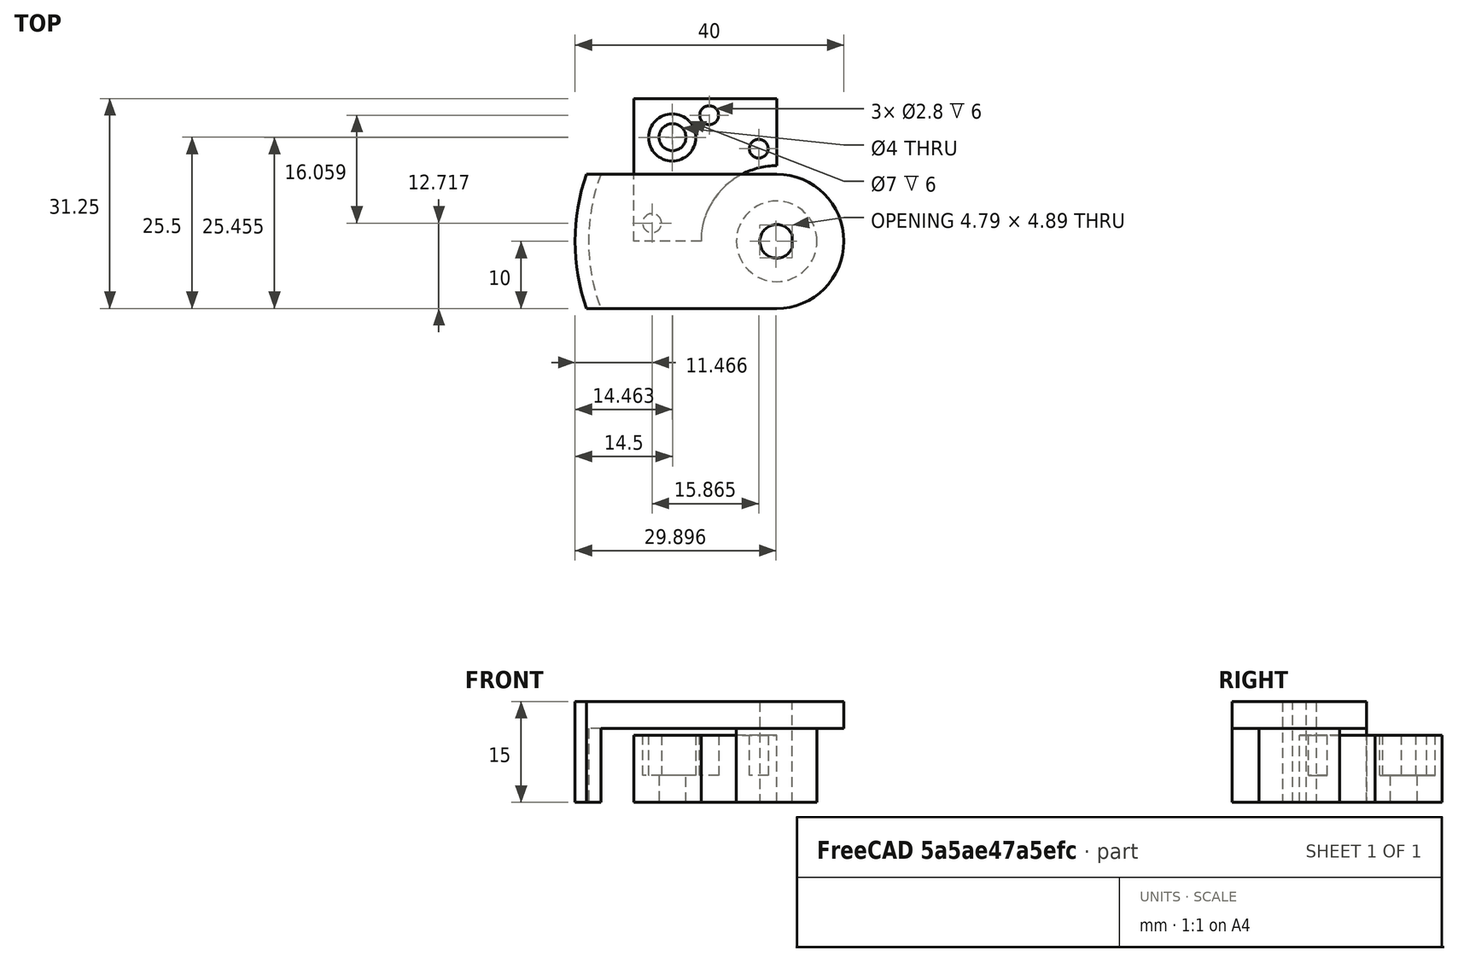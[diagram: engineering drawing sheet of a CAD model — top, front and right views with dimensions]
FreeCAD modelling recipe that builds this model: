
FCSTD DOCUMENT  (FreeCAD 0.19R)
Label: False_zaxisFlag
License: All rights reserved
LicenseURL: http://en.wikipedia.org/wiki/All_rights_reserved
objects: Sketcher::SketchObject×6, PartDesign::Pocket×3, PartDesign::Pad×2, PartDesign::Body×2, Mesh::Feature×2
note: 18 computed .brp shape members not serialized (recipe doc carries the construction recipe); baked Part::Feature solids carry a one-line shape summary decoded from their .brp

FEATURE [Sketcher::SketchObject] Sketch
  FullyConstrained = true
  MapMode = 5
  Support = -> [XY_Plane]
  sketch-geometry (6):
    g0: ArcOfCircle CenterX=0 CenterY=0 CenterZ=0 NormalX=0 NormalY=0 NormalZ=1 AngleXU=0 Radius=11.25 StartAngle=1.5708 EndAngle=3.14159
    g1: LineSegment StartX=-11.25 StartY=1.4e-15 StartZ=0 EndX=-21.25 EndY=0 EndZ=0
    g2: LineSegment StartX=-21.25 StartY=0 StartZ=0 EndX=-21.25 EndY=21.25 EndZ=0
    g3: LineSegment StartX=-21.25 StartY=21.25 StartZ=0 EndX=0 EndY=21.25 EndZ=0
    g4: LineSegment StartX=0 StartY=21.25 StartZ=0 EndX=7e-16 EndY=11.25 EndZ=0
    g5: Circle CenterX=-15.5 CenterY=15.5 CenterZ=0 NormalX=0 NormalY=0 NormalZ=1 AngleXU=0 Radius=2
  constraints (18):
    c: Coincident(g0,g-1)
    c: PointOnObject(g0,g-2)
    c: PointOnObject(g0,g-1)
    c: Coincident(g0,g1)
    c: Coincident(g1,g2)
    c: Vertical(g2)
    c: Coincident(g2,g3)
    c: PointOnObject(g3,g-2)
    c: Horizontal(g3)
    c: Coincident(g3,g4)
    c: Coincident(g4,g0)
    c: Diameter(g0) = 22.5
    c: Distance(g4) = 10
    c: Distance(g1) = 10
    c: PointOnObject(g1,g-1)
    c: DistanceX(g5) = -15.5
    c: DistanceY(g5) = 15.5
    c: Diameter(g5) = 4
FEATURE [PartDesign::Pad] Pad
  Direction = (1,1,1)
  Length = 10
  Length2 = 100
  Profile = -> Sketch
  Type = 0
FEATURE [Sketcher::SketchObject] Sketch001
  FullyConstrained = false
  MapMode = 5
  Placement = pos=(0,0,10) rot=(0,0,1;0rad)
  Support = -> [Pad]
  sketch-geometry (4):
    g0: LineSegment StartX=-19.7905 StartY=5 StartZ=0 EndX=-14.7905 EndY=5 EndZ=0
    g1: LineSegment StartX=-14.7905 StartY=5 StartZ=0 EndX=-14.7905 EndY=0 EndZ=0
    g2: LineSegment StartX=-14.7905 StartY=0 StartZ=0 EndX=-19.7905 EndY=0 EndZ=0
    g3: LineSegment StartX=-19.7905 StartY=0 StartZ=0 EndX=-19.7905 EndY=5 EndZ=0
  constraints (11):
    c: Coincident(g0,g1)
    c: Coincident(g1,g2)
    c: Coincident(g2,g3)
    c: Coincident(g3,g0)
    c: Horizontal(g0)
    c: Horizontal(g2)
    c: Vertical(g1)
    c: Vertical(g3)
    c: PointOnObject(g1,g-1)
    c: Distance(g0) = 5
    c: Distance(g1) = 5
FEATURE [Sketcher::SketchObject] Sketch002
  FullyConstrained = false
  MapMode = 5
  Placement = pos=(0,0,10) rot=(0,0,1;0rad)
  Support = -> [Pad]
  sketch-geometry (4):
    g0: Circle CenterX=-18.5342 CenterY=2.71688 CenterZ=0 NormalX=0 NormalY=0 NormalZ=1 AngleXU=0 Radius=1.4
    g1: Circle CenterX=-10.0417 CenterY=18.7754 CenterZ=0 NormalX=0 NormalY=0 NormalZ=1 AngleXU=0 Radius=1.4
    g2: Circle CenterX=-2.66872 CenterY=13.7957 CenterZ=0 NormalX=0 NormalY=0 NormalZ=1 AngleXU=0 Radius=1.4
    g3: Circle CenterX=-15.5368 CenterY=15.4549 CenterZ=0 NormalX=0 NormalY=0 NormalZ=1 AngleXU=0 Radius=3.5
  constraints (4):
    c: Diameter(g0) = 2.8
    c: Equal(g0,g2)
    c: Equal(g0,g1)
    c: Diameter(g3) = 7
FEATURE [PartDesign::Pocket] Pocket
  BaseFeature = -> Pad
  Length = 6
  Length2 = 100
  Profile = -> Sketch002
  Type = 0
FEATURE [PartDesign::Body] Body
  Group = -> [Sketch,Pad,Sketch001,Sketch002,Pocket]
  Origin = -> Origin
  Tip = -> Pocket
FEATURE [Mesh::Feature] Mesh  label="Pocket (Meshed)"
FEATURE [Sketcher::SketchObject] Sketch003
  FullyConstrained = true
  MapMode = 5
  Support = -> [XY_Plane001]
  sketch-geometry (4):
    g0: ArcOfCircle CenterX=0 CenterY=0 CenterZ=0 NormalX=0 NormalY=0 NormalZ=1 AngleXU=0 Radius=10 StartAngle=4.71239 EndAngle=7.85398
    g1: LineSegment StartX=-1.8e-15 StartY=-10 StartZ=0 EndX=-28.2843 EndY=-10 EndZ=0
    g2: LineSegment StartX=3.1e-15 StartY=10 StartZ=0 EndX=-28.2843 EndY=10 EndZ=0
    g3: ArcOfCircle CenterX=0 CenterY=0 CenterZ=0 NormalX=0 NormalY=0 NormalZ=1 AngleXU=0 Radius=30 StartAngle=2.80176 EndAngle=3.48143
  constraints (12):
    c: Coincident(g0,g-1)
    c: PointOnObject(g0,g-2)
    c: PointOnObject(g0,g-2)
    c: Coincident(g1,g0)
    c: Horizontal(g1)
    c: Coincident(g2,g0)
    c: Horizontal(g2)
    c: Coincident(g3,g0)
    c: Coincident(g3,g1)
    c: Coincident(g3,g2)
    c: Radius(g3) = 30
    c: Radius(g0) = 10
FEATURE [PartDesign::Pad] Pad001
  Direction = (1,1,1)
  Length = 15
  Length2 = 100
  Profile = -> Sketch003
  Type = 0
FEATURE [Sketcher::SketchObject] Sketch004
  FullyConstrained = true
  MapMode = 5
  Placement = pos=(0,0,0) rot=(1,0,0;3.14159rad)
  Support = -> [Pad001]
  sketch-geometry (2):
    g0: Circle CenterX=0 CenterY=0 CenterZ=0 NormalX=0 NormalY=0 NormalZ=1 AngleXU=0 Radius=28
    g1: Circle CenterX=0 CenterY=0 CenterZ=0 NormalX=0 NormalY=0 NormalZ=1 AngleXU=0 Radius=6
  constraints (4):
    c: Coincident(g0,g-1)
    c: Coincident(g1,g0)
    c: Radius(g0) = 28
    c: Radius(g1) = 6
FEATURE [PartDesign::Pocket] Pocket001
  BaseFeature = -> Pad001
  Length = 11
  Length2 = 100
  Profile = -> Sketch004
  Type = 0
FEATURE [Sketcher::SketchObject] Sketch005
  FullyConstrained = true
  MapMode = 5
  Placement = pos=(0,0,0) rot=(1,0,0;3.14159rad)
  Support = -> [Pocket001]
  sketch-geometry (2):
    g0: ArcOfCircle CenterX=0 CenterY=0 CenterZ=0 NormalX=0 NormalY=0 NormalZ=1 AngleXU=0 Radius=2.5 StartAngle=0.411517 EndAngle=5.87167
    g1: LineSegment StartX=2.29129 StartY=-1 StartZ=0 EndX=2.29129 EndY=1 EndZ=0
  constraints (6):
    c: Coincident(g0,g-1)
    c: Coincident(g1,g0)
    c: Coincident(g1,g0)
    c: Diameter(g0) = 5
    c: Distance(g1) = 2
    c: Vertical(g1)
FEATURE [PartDesign::Pocket] Pocket002
  BaseFeature = -> Pocket001
  Length = 5
  Length2 = 100
  Profile = -> Sketch005
  Type = 1
FEATURE [PartDesign::Body] Body001
  Group = -> [Sketch003,Pad001,Sketch004,Pocket001,Sketch005,Pocket002]
  Origin = -> Origin001
  Tip = -> Pocket002
FEATURE [Mesh::Feature] Mesh001  label="Pocket002 (Meshed)"
